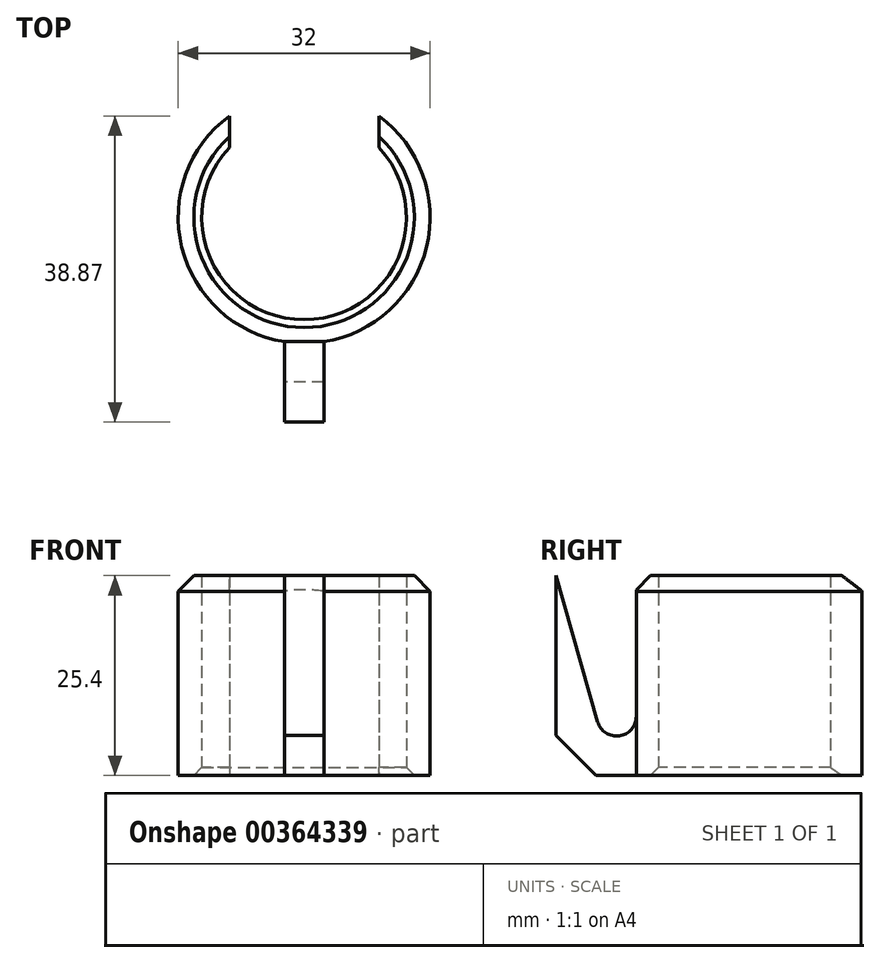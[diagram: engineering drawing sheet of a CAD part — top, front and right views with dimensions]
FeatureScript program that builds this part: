
annotation { "Feature Type Name" : "Feature", "Feature Type Description" : "" }
export const myFeature = defineFeature(function(context is Context, id is Id, definition is map)
    precondition{}
    {
        {
            var Q0;
            Q0=qCreatedBy(makeId("Top.planeOp"),FACE);
            var sketch = newSketch(context, id + "F0", { "sketchPlane" : qUnion([Q0])});
            skCircle(sketch, "E0", {"center": v(0, 0) * mm, "radius": 9.5 * mm});
            skCircle(sketch, "E1", {"center": v(0, 0) * mm, "radius": 13 * mm});
            skLineSegment(sketch, "E2", {"start": v(-9.5, 0) * mm, "end": v(-9.5, 12.87) * mm});
            skLineSegment(sketch, "E3", {"start": v(9.5, 0) * mm, "end": v(9.5, 12.87) * mm});
            skCircle(sketch, "E4", {"center": v(0, 0) * mm, "radius": 16 * mm});
            skSolve(sketch);
        }
        {
            var Q0;
            {var subQ0=sQuery(id+"F0.wireOp",EDGE,"E2");var subQ1=sQuery(id+"F0.wireOp",EDGE,"E1");var subQ2=makeQuery(id+"F0.imprint","INTERSECT",VERTEX,{"derivedFrom":[subQ1,subQ0]});Q0=makeQuery(id+"F0.imprint","IMPRINT",FACE,{"disambiguationData":[TD([[makeQuery(id+"F0.imprint","IMPRINT",EDGE,{"disambiguationData":[TD([[subQ2,-1.0]])],"derivedFrom":subQ1}),-1.0]])]});}
            extrude(context, id + "F1", {"entities" : qUnion([Q0]), "depth" : 25.4 * mm});
        }
        {
            var Q0;
            Q0=makeQuery(id+"F1.opExtrude","CAP_FACE",FACE,{"disambiguationData":[OSD([sQuery(id+"F0.wireOp",EDGE,"E1"),sQuery(id+"F0.wireOp",EDGE,"E2"),sQuery(id+"F0.wireOp",EDGE,"E3"),sQuery(id+"F0.wireOp",EDGE,"E4")])],"isStart":true});
            var sketch = newSketch(context, id + "F2", { "sketchPlane" : qUnion([Q0])});
            skLineSegment(sketch, "E5.bottom", {"start": v(2.5, 26) * mm, "end": v(-2.5, 26) * mm});
            skLineSegment(sketch, "E5.top", {"start": v(2.5, -26) * mm, "end": v(-2.5, -26) * mm});
            skLineSegment(sketch, "E5.left", {"start": v(2.5, 26) * mm, "end": v(2.5, -26) * mm});
            skLineSegment(sketch, "E5.right", {"start": v(-2.5, 26) * mm, "end": v(-2.5, -26) * mm});
            skPoint(sketch, "E5.middle", {"position": v(0, 0) * mm});
            skSolve(sketch);
        }
        {
            var Q0;
            {var subQ0=sQuery(id+"F2.wireOp",EDGE,"E5.bottom");Q0=makeQuery(id+"F2.imprint","IMPRINT",FACE,{"disambiguationData":[TD([[makeQuery(id+"F2.imprint","IMPRINT",EDGE,{"derivedFrom":subQ0}),1.0]])]});}
            var Q1;
            Q1=makeQuery(id+"F1.opExtrude","CAP_FACE",FACE,{"disambiguationData":[OSD([sQuery(id+"F0.wireOp",EDGE,"E1"),sQuery(id+"F0.wireOp",EDGE,"E2"),sQuery(id+"F0.wireOp",EDGE,"E3"),sQuery(id+"F0.wireOp",EDGE,"E4")])],"isStart":false});
            extrude(context, id + "F3", {"entities" : qUnion([Q0]), "operationType" : NewBodyOperationType.ADD, "endBound" : BoundingType.UP_TO_SURFACE, "oppositeDirection" : true, "endBoundEntityFace" : qUnion([Q1]), "depth" : 25.4 * mm});
        }
        {
            var Q0;
            Q0=makeQuery(id+"F3.opExtrude","SWEPT_FACE",FACE,{"disambiguationData":[OSD([sQuery(id+"F2.wireOp",EDGE,"E5.right")])]});
            var sketch = newSketch(context, id + "F4", { "sketchPlane" : qUnion([Q0])});
            skCircle(sketch, "E6", {"center": v(18.3, 7.5) * mm, "radius": 2.5 * mm});
            skLineSegment(sketch, "E7", {"start": v(26, 25.4) * mm, "end": v(20.7, 6.82) * mm});
            skSolve(sketch);
        }
        {
            var Q0;
            {var subQ0=sQuery(id+"F4.wireOp",EDGE,"E7");Q0=makeQuery(id+"F4.imprint","IMPRINT",FACE,{"disambiguationData":[TD([[makeQuery(id+"F4.imprint","IMPRINT",EDGE,{"derivedFrom":subQ0}),-1.0]])]});}
            var Q1;
            {var subQ0=sQuery(id+"F4.wireOp",EDGE,"E6");var subQ1=makeQuery(id+"F4.imprint","INTERSECT",VERTEX,{"derivedFrom":[subQ0,sQuery(id+"F4.wireOp",EDGE,"E7")]});Q1=makeQuery(id+"F4.imprint","IMPRINT",FACE,{"disambiguationData":[TD([[makeQuery(id+"F4.imprint","IMPRINT",EDGE,{"disambiguationData":[TD([[subQ1,1.0]])],"derivedFrom":subQ0}),1.0]])]});}
            extrude(context, id + "F5", {"entities" : qUnion([Q0, Q1]), "operationType" : NewBodyOperationType.REMOVE, "oppositeDirection" : true, "depth" : 25.4 * mm});
        }
        {
            var Q0;
            Q0=makeQuery(id+"F3.opExtrude","CAP_EDGE",EDGE,{"disambiguationData":[OSD([sQuery(id+"F2.wireOp",EDGE,"E5.bottom")])],"isStart":true});
            chamfer(context, id + "F6", {"entities" : qUnion([Q0]), "width" : 5.08 * mm, "tangentPropagation" : true});
        }
        {
            var Q0;
            Q0=makeQuery(id+"F1.opExtrude","CAP_EDGE",EDGE,{"disambiguationData":[OSD([sQuery(id+"F0.wireOp",EDGE,"E1")])],"isStart":true});
            chamfer(context, id + "F7", {"entities" : qUnion([Q0]), "width" : 1 * mm, "tangentPropagation" : true});
        }
        {
            var Q0;
            {var subQ0=sQuery(id+"F0.wireOp",EDGE,"E4");var subQ2=sQuery(id+"F0.wireOp",EDGE,"E2");Q0=makeQuery(id+"F3.boolean.opBoolean","SPLIT",EDGE,{"disambiguationData":[TD([makeQuery(id+"F1.opExtrude","SWEPT_FACE",FACE,{"disambiguationData":[OSD([subQ2])]})])],"derivedFrom":makeQuery(id+"F1.opExtrude","CAP_EDGE",EDGE,{"disambiguationData":[OSD([subQ0])],"isStart":false})});}
            chamfer(context, id + "F8", {"entities" : qUnion([Q0]), "width" : 2 * mm, "tangentPropagation" : true});
        }
    });
